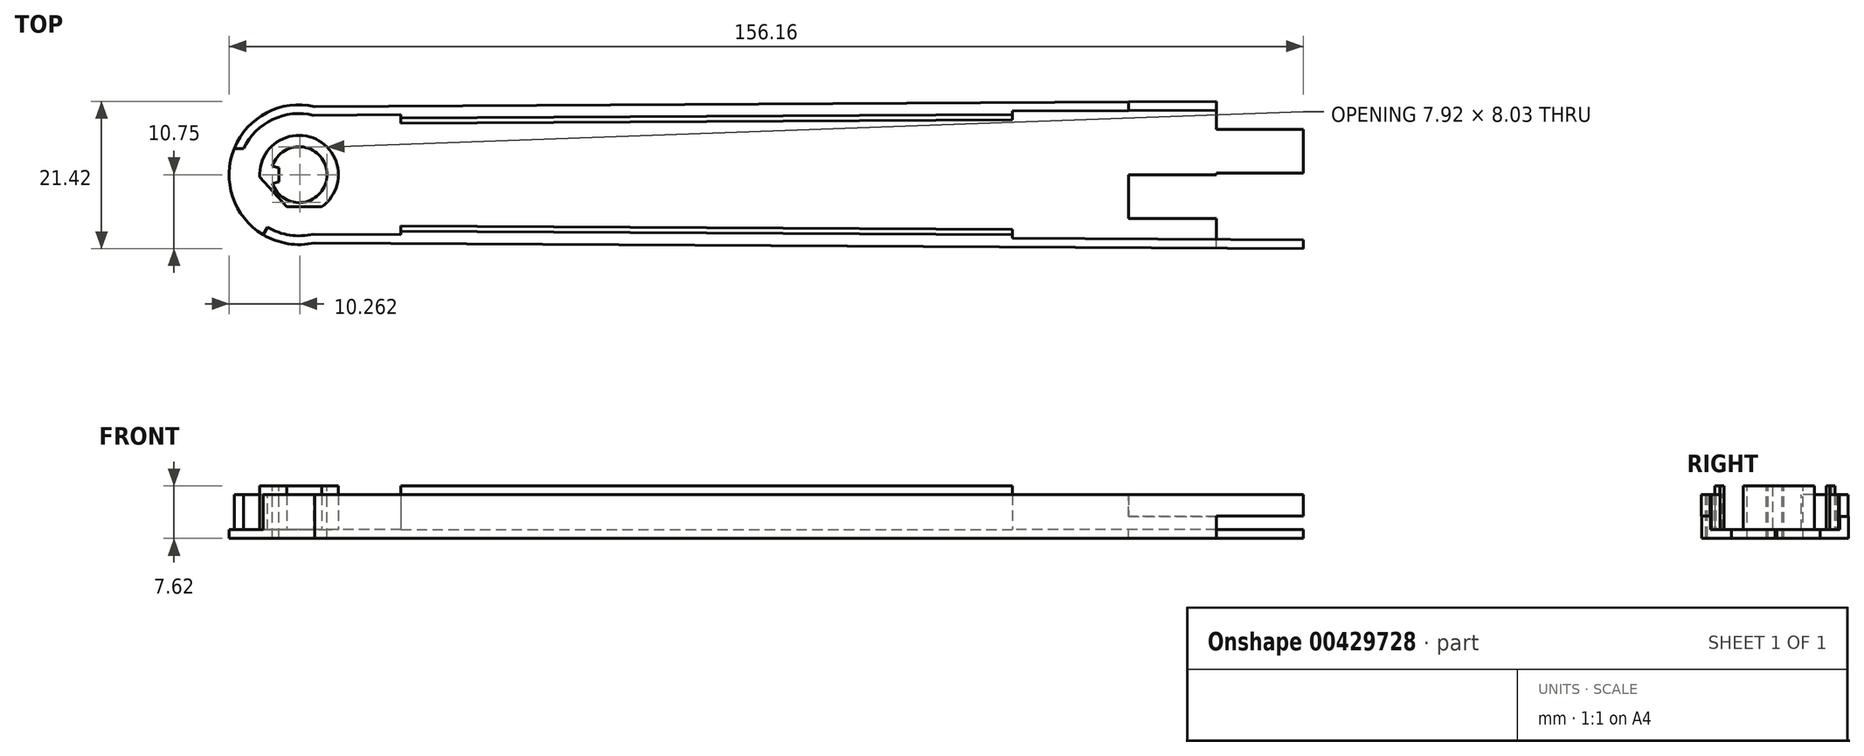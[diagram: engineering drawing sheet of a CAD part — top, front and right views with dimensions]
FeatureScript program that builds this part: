
annotation { "Feature Type Name" : "Feature", "Feature Type Description" : "" }
export const myFeature = defineFeature(function(context is Context, id is Id, definition is map)
    precondition{}
    {
        {
            var Q0;
            Q0=qCreatedBy(makeId("Top.planeOp"),FACE);
            var sketch = newSketch(context, id + "F0", { "sketchPlane" : qUnion([Q0])});
            skPoint(sketch, "E0", {"position": v(-133.35, 0) * mm});
            skPoint(sketch, "E1", {"position": v(133.35, 0) * mm});
            skCircle(sketch, "E2", {"center": v(-133.35, 0) * mm, "radius": 10.16 * mm});
            skCircle(sketch, "E3", {"center": v(133.35, 0) * mm, "radius": 12.07 * mm});
            skPoint(sketch, "E4", {"position": v(-131.1, 9.9) * mm});
            skPoint(sketch, "E5", {"position": v(-131.1, -9.9) * mm});
            skPoint(sketch, "E6", {"position": v(129.49, 11.43) * mm});
            skPoint(sketch, "E7", {"position": v(129.49, -11.43) * mm});
            skLineSegment(sketch, "E8", {"start": v(129.49, 11.43) * mm, "end": v(-131.1, 9.9) * mm});
            skLineSegment(sketch, "E9", {"start": v(129.49, -11.43) * mm, "end": v(-131.1, -9.9) * mm});
            skPoint(sketch, "E10", {"position": v(0, 21.22) * mm});
            skPoint(sketch, "E11", {"position": v(0, -23.02) * mm});
            skLineSegment(sketch, "E12", {"start": v(0, 21.22) * mm, "end": v(0, -23.02) * mm});
            skSolve(sketch);
        }
        {
            var Q0;
            {var subQ0=sQuery(id+"F0.wireOp",EDGE,"E2");var subQ1=makeQuery(id+"F0.imprint","INTERSECT",VERTEX,{"derivedFrom":[subQ0,sQuery(id+"F0.wireOp",EDGE,"E8")]});Q0=makeQuery(id+"F0.imprint","IMPRINT",FACE,{"disambiguationData":[TD([[makeQuery(id+"F0.imprint","IMPRINT",EDGE,{"disambiguationData":[TD([[subQ1,-1.0]])],"derivedFrom":subQ0}),1.0]])]});}
            var Q1;
            {var subQ0=sQuery(id+"F0.wireOp",EDGE,"E8");var subQ1=sQuery(id+"F0.wireOp",EDGE,"E2");var subQ2=makeQuery(id+"F0.imprint","INTERSECT",VERTEX,{"derivedFrom":[subQ1,subQ0]});Q1=makeQuery(id+"F0.imprint","IMPRINT",FACE,{"disambiguationData":[TD([[makeQuery(id+"F0.imprint","IMPRINT",EDGE,{"disambiguationData":[TD([[subQ2,1.0]])],"derivedFrom":subQ1}),-1.0]])]});}
            extrude(context, id + "F1", {"entities" : qUnion([Q0, Q1]), "depth" : 6.35 * mm});
        }
        {
            var Q0;
            Q0=makeQuery(id+"F1.opExtrude","CAP_FACE",FACE,{"disambiguationData":[OSD([sQuery(id+"F0.wireOp",EDGE,"E2"),sQuery(id+"F0.wireOp",EDGE,"E8"),sQuery(id+"F0.wireOp",EDGE,"E9"),sQuery(id+"F0.wireOp",EDGE,"E12")])],"isStart":false});
            var Q1;
            Q1=makeQuery(id+"F1.opExtrude","SWEPT_FACE",FACE,{"disambiguationData":[OSD([sQuery(id+"F0.wireOp",EDGE,"E12")])]});
            shell(context, id + "F2", {"entities" : qUnion([Q0, Q1]), "thickness" : 1.27 * mm});
        }
        {
            var Q0;
            Q0=makeQuery(id+"F2.opShell","OFFSET_FACE",FACE,{"disambiguationData":[OSD([sQuery(id+"F0.wireOp",EDGE,"E2"),sQuery(id+"F0.wireOp",EDGE,"E8"),sQuery(id+"F0.wireOp",EDGE,"E9"),sQuery(id+"F0.wireOp",EDGE,"E12")])]});
            var sketch = newSketch(context, id + "F3", { "sketchPlane" : qUnion([Q0])});
            skLineSegment(sketch, "E13.bottom", {"start": v(0, 0) * mm, "end": v(-12.75, 0) * mm});
            skLineSegment(sketch, "E13.top", {"start": v(0, -6.35) * mm, "end": v(-12.75, -6.35) * mm});
            skLineSegment(sketch, "E13.left", {"start": v(0, 0) * mm, "end": v(0, -6.35) * mm});
            skLineSegment(sketch, "E13.right", {"start": v(-12.75, 0) * mm, "end": v(-12.75, -6.35) * mm});
            skSolve(sketch);
        }
        {
            var Q0;
            Q0=makeQuery(id+"F3.imprint","IMPRINT",FACE,{"disambiguationData":[TD([[makeQuery(id+"F3.imprint","IMPRINT",EDGE,{"derivedFrom":sQuery(id+"F3.wireOp",EDGE,"E13.bottom")}),1.0]])]});
            extrude(context, id + "F4", {"entities" : qUnion([Q0]), "operationType" : NewBodyOperationType.REMOVE, "oppositeDirection" : true, "depth" : 25.4 * mm});
        }
        {
            var Q0;
            Q0=makeQuery(id+"F2.opShell","OFFSET_FACE",FACE,{"disambiguationData":[OSD([sQuery(id+"F0.wireOp",EDGE,"E2"),sQuery(id+"F0.wireOp",EDGE,"E8"),sQuery(id+"F0.wireOp",EDGE,"E9"),sQuery(id+"F0.wireOp",EDGE,"E12")])]});
            var sketch = newSketch(context, id + "F5", { "sketchPlane" : qUnion([Q0])});
            skPoint(sketch, "E14", {"position": v(0, 0.25) * mm});
            skLineSegment(sketch, "E15.bottom", {"start": v(0, 0.25) * mm, "end": v(12.65, 0.25) * mm});
            skLineSegment(sketch, "E15.top", {"start": v(0, 6.58) * mm, "end": v(12.65, 6.58) * mm});
            skLineSegment(sketch, "E15.left", {"start": v(0, 0.25) * mm, "end": v(0, 6.58) * mm});
            skLineSegment(sketch, "E15.right", {"start": v(12.65, 0.25) * mm, "end": v(12.65, 6.58) * mm});
            skSolve(sketch);
        }
        {
            var Q0;
            Q0=makeQuery(id+"F5.imprint","IMPRINT",FACE,{"disambiguationData":[TD([[makeQuery(id+"F5.imprint","IMPRINT",EDGE,{"derivedFrom":sQuery(id+"F5.wireOp",EDGE,"E15.bottom")}),1.0]])]});
            extrude(context, id + "F6", {"entities" : qUnion([Q0]), "operationType" : NewBodyOperationType.ADD, "oppositeDirection" : true, "depth" : 1.27 * mm});
        }
        {
            var Q0;
            Q0=makeQuery(id+"F2.opShell","OFFSET_FACE",FACE,{"disambiguationData":[OSD([sQuery(id+"F0.wireOp",EDGE,"E9")])]});
            var sketch = newSketch(context, id + "F7", { "sketchPlane" : qUnion([Q0])});
            skLineSegment(sketch, "E16.bottom", {"start": v(-0.05, 6.35) * mm, "end": v(-12.7, 6.35) * mm});
            skLineSegment(sketch, "E16.top", {"start": v(-0.05, 3.23) * mm, "end": v(-12.7, 3.23) * mm});
            skLineSegment(sketch, "E16.left", {"start": v(-0.05, 6.35) * mm, "end": v(-0.05, 3.23) * mm});
            skLineSegment(sketch, "E16.right", {"start": v(-12.7, 6.35) * mm, "end": v(-12.7, 3.23) * mm});
            skSolve(sketch);
        }
        {
            var Q0;
            Q0=makeQuery(id+"F7.imprint","IMPRINT",FACE,{"disambiguationData":[TD([[makeQuery(id+"F7.imprint","IMPRINT",EDGE,{"derivedFrom":sQuery(id+"F7.wireOp",EDGE,"E16.bottom")}),1.0]])]});
            extrude(context, id + "F8", {"entities" : qUnion([Q0]), "operationType" : NewBodyOperationType.ADD, "oppositeDirection" : true, "depth" : 1.27 * mm});
        }
        {
            var Q0;
            Q0=makeQuery(id+"F1.opExtrude","SWEPT_FACE",FACE,{"disambiguationData":[OSD([sQuery(id+"F0.wireOp",EDGE,"E8")])]});
            var sketch = newSketch(context, id + "F9", { "sketchPlane" : qUnion([Q0])});
            skLineSegment(sketch, "E17.bottom", {"start": v(-0.06, 6.35) * mm, "end": v(12.69, 6.35) * mm});
            skLineSegment(sketch, "E17.top", {"start": v(-0.06, 3.18) * mm, "end": v(12.69, 3.18) * mm});
            skLineSegment(sketch, "E17.left", {"start": v(-0.06, 6.35) * mm, "end": v(-0.06, 3.18) * mm});
            skLineSegment(sketch, "E17.right", {"start": v(12.69, 6.35) * mm, "end": v(12.69, 3.18) * mm});
            skSolve(sketch);
        }
        {
            var Q0;
            Q0=makeQuery(id+"F9.imprint","IMPRINT",FACE,{"disambiguationData":[TD([[makeQuery(id+"F9.imprint","IMPRINT",EDGE,{"derivedFrom":sQuery(id+"F9.wireOp",EDGE,"E17.bottom")}),-1.0]])]});
            extrude(context, id + "F10", {"entities" : qUnion([Q0]), "operationType" : NewBodyOperationType.REMOVE, "oppositeDirection" : true, "depth" : 2.54 * mm});
        }
        {
            var Q0;
            Q0=makeQuery(id+"F6.boolean.opBoolean","MERGE",FACE,{"derivedFrom":[makeQuery(id+"F2.opShell","OFFSET_FACE",FACE,{"disambiguationData":[OSD([sQuery(id+"F0.wireOp",EDGE,"E2"),sQuery(id+"F0.wireOp",EDGE,"E8"),sQuery(id+"F0.wireOp",EDGE,"E9"),sQuery(id+"F0.wireOp",EDGE,"E12")])]}),makeQuery(id+"F6.opExtrude","CAP_FACE",FACE,{"disambiguationData":[OSD([sQuery(id+"F5.wireOp",EDGE,"E15.bottom"),sQuery(id+"F5.wireOp",EDGE,"E15.top"),sQuery(id+"F5.wireOp",EDGE,"E15.left"),sQuery(id+"F5.wireOp",EDGE,"E15.right")])],"isStart":true})]});
            var sketch = newSketch(context, id + "F11", { "sketchPlane" : qUnion([Q0])});
            skLineSegment(sketch, "E18", {"start": v(-118.54, 8.7) * mm, "end": v(-29.64, 9.23) * mm});
            skLineSegment(sketch, "E19", {"start": v(-118.54, 7.44) * mm, "end": v(-29.64, 7.96) * mm});
            skLineSegment(sketch, "E20", {"start": v(-29.64, 7.96) * mm, "end": v(-29.64, 9.23) * mm});
            skLineSegment(sketch, "E21", {"start": v(-118.54, 7.44) * mm, "end": v(-118.54, 8.7) * mm});
            skLineSegment(sketch, "E22", {"start": v(-118.54, -8.7) * mm, "end": v(-29.64, -9.23) * mm});
            skLineSegment(sketch, "E23", {"start": v(-118.54, -7.44) * mm, "end": v(-29.64, -7.96) * mm});
            skLineSegment(sketch, "E24", {"start": v(-118.54, -7.44) * mm, "end": v(-118.54, -8.7) * mm});
            skLineSegment(sketch, "E25", {"start": v(-29.64, -7.96) * mm, "end": v(-29.64, -9.23) * mm});
            skSolve(sketch);
        }
        {
            var Q0;
            Q0=makeQuery(id+"F11.imprint","IMPRINT",FACE,{"disambiguationData":[TD([[makeQuery(id+"F11.imprint","IMPRINT",EDGE,{"derivedFrom":sQuery(id+"F11.wireOp",EDGE,"E18")}),1.0]])]});
            var Q1;
            Q1=makeQuery(id+"F11.imprint","IMPRINT",FACE,{"disambiguationData":[TD([[makeQuery(id+"F11.imprint","IMPRINT",EDGE,{"derivedFrom":sQuery(id+"F11.wireOp",EDGE,"E22")}),-1.0]])]});
            extrude(context, id + "F12", {"entities" : qUnion([Q0, Q1]), "operationType" : NewBodyOperationType.ADD, "depth" : 5.08 * mm});
        }
        {
            var Q0;
            Q0=makeQuery(id+"F6.boolean.opBoolean","MERGE",FACE,{"derivedFrom":[makeQuery(id+"F2.opShell","OFFSET_FACE",FACE,{"disambiguationData":[OSD([sQuery(id+"F0.wireOp",EDGE,"E2"),sQuery(id+"F0.wireOp",EDGE,"E8"),sQuery(id+"F0.wireOp",EDGE,"E9"),sQuery(id+"F0.wireOp",EDGE,"E12")])]}),makeQuery(id+"F6.opExtrude","CAP_FACE",FACE,{"disambiguationData":[OSD([sQuery(id+"F5.wireOp",EDGE,"E15.bottom"),sQuery(id+"F5.wireOp",EDGE,"E15.top"),sQuery(id+"F5.wireOp",EDGE,"E15.left"),sQuery(id+"F5.wireOp",EDGE,"E15.right")])],"isStart":true})]});
            var sketch = newSketch(context, id + "F13", { "sketchPlane" : qUnion([Q0])});
            skCircle(sketch, "E26", {"center": v(-133.35, 0) * mm, "radius": 5.72 * mm});
            skPoint(sketch, "E27", {"position": v(-139.05, -0.34) * mm});
            skPoint(sketch, "E28", {"position": v(-130.02, -4.65) * mm});
            skPoint(sketch, "E29", {"position": v(-135.1, -4.65) * mm});
            skLineSegment(sketch, "E30", {"start": v(-139.05, -0.34) * mm, "end": v(-135.1, -4.65) * mm});
            skLineSegment(sketch, "E31", {"start": v(-135.1, -4.65) * mm, "end": v(-130.02, -4.65) * mm});
            skCircle(sketch, "E32", {"center": v(-133.35, 0) * mm, "radius": 4.06 * mm});
            skSolve(sketch);
        }
        {
            var Q0;
            {var subQ0=sQuery(id+"F13.wireOp",EDGE,"E30");Q0=makeQuery(id+"F13.imprint","IMPRINT",FACE,{"disambiguationData":[TD([[makeQuery(id+"F13.imprint","IMPRINT",EDGE,{"derivedFrom":subQ0}),1.0]])]});}
            var Q1;
            Q1=makeQuery(id+"F13.imprint","IMPRINT",FACE,{"disambiguationData":[TD([[makeQuery(id+"F13.imprint","IMPRINT",EDGE,{"derivedFrom":sQuery(id+"F13.wireOp",EDGE,"E32")}),1.0]])]});
            extrude(context, id + "F14", {"entities" : qUnion([Q0, Q1]), "operationType" : NewBodyOperationType.ADD, "depth" : 6.35 * mm});
        }
        {
            var Q0;
            Q0=makeQuery(id+"F14.opExtrude","CAP_FACE",FACE,{"disambiguationData":[OSD([sQuery(id+"F13.wireOp",EDGE,"E26"),sQuery(id+"F13.wireOp",EDGE,"KSTsQ0zC-PDxz-6PK0-GiVB-AzygPapndajD"),sQuery(id+"F13.wireOp",EDGE,"wdBHU8a3-bk62-31aO-teXj-baJQRgUME3HU")])],"isStart":false});
            var sketch = newSketch(context, id + "F15", { "sketchPlane" : qUnion([Q0])});
            skCircle(sketch, "E33", {"center": v(-133.35, 0) * mm, "radius": 4.06 * mm});
            skPoint(sketch, "E34", {"position": v(-137.21, 1.27) * mm});
            skPoint(sketch, "E35", {"position": v(-137.21, -1.27) * mm});
            skPoint(sketch, "E36", {"position": v(-136.25, 1.02) * mm});
            skPoint(sketch, "E37", {"position": v(-136.25, -1.02) * mm});
            skLineSegment(sketch, "E38", {"start": v(-137.21, 1.27) * mm, "end": v(-136.25, 1.02) * mm});
            skLineSegment(sketch, "E39", {"start": v(-136.25, 1.02) * mm, "end": v(-136.25, -1.02) * mm});
            skLineSegment(sketch, "E40", {"start": v(-137.21, -1.27) * mm, "end": v(-136.25, -1.02) * mm});
            skSolve(sketch);
        }
        {
            var Q0;
            {var subQ0=sQuery(id+"F15.wireOp",EDGE,"E38");Q0=makeQuery(id+"F15.imprint","IMPRINT",FACE,{"disambiguationData":[TD([[makeQuery(id+"F15.imprint","IMPRINT",EDGE,{"derivedFrom":subQ0}),1.0]])]});}
            extrude(context, id + "F16", {"entities" : qUnion([Q0]), "operationType" : NewBodyOperationType.REMOVE, "oppositeDirection" : true, "depth" : 25.4 * mm});
        }
        {
            var Q0;
            Q0=makeQuery(id+"F8.boolean.opBoolean","MERGE",FACE,{"derivedFrom":[makeQuery(id+"F1.opExtrude","CAP_FACE",FACE,{"disambiguationData":[OSD([sQuery(id+"F0.wireOp",EDGE,"E2"),sQuery(id+"F0.wireOp",EDGE,"E8"),sQuery(id+"F0.wireOp",EDGE,"E9"),sQuery(id+"F0.wireOp",EDGE,"E12")])],"isStart":false}),makeQuery(id+"F8.opExtrude","SWEPT_FACE",FACE,{"disambiguationData":[OSD([sQuery(id+"F7.wireOp",EDGE,"E16.bottom")])]})]});
            var sketch = newSketch(context, id + "F17", { "sketchPlane" : qUnion([Q0])});
            skPoint(sketch, "E41", {"position": v(-141.38, 3.8) * mm});
            skPoint(sketch, "E42", {"position": v(-137.93, -7.62) * mm});
            skPoint(sketch, "E43", {"position": v(-142.77, 3.8) * mm});
            skPoint(sketch, "E44", {"position": v(-138.58, -8.7) * mm});
            skPoint(sketch, "E45", {"position": v(-133.35, 0) * mm});
            skLineSegment(sketch, "E46", {"start": v(-133.35, 0) * mm, "end": v(-138.58, -8.7) * mm});
            skLineSegment(sketch, "E47", {"start": v(-141.38, 3.8) * mm, "end": v(-142.77, 3.8) * mm});
            skArc(sketch, "E48", {"start": v(-141.38, 3.8) * mm, "mid": v(-141.86, -2.57) * mm, "end": v(-137.93, -7.62) * mm});
            skArc(sketch, "E49", {"start": v(-142.77, 3.8) * mm, "mid": v(-142.99, -3.22) * mm, "end": v(-138.58, -8.7) * mm});
            skSolve(sketch);
        }
        {
            var Q0;
            Q0=makeQuery(id+"F17.imprint","IMPRINT",FACE,{"disambiguationData":[TD([[makeQuery(id+"F17.imprint","IMPRINT",EDGE,{"derivedFrom":sQuery(id+"F17.wireOp",EDGE,"E47")}),1.0]])]});
            var Q1;
            Q1=makeQuery(id+"F6.boolean.opBoolean","MERGE",FACE,{"derivedFrom":[makeQuery(id+"F2.opShell","OFFSET_FACE",FACE,{"disambiguationData":[OSD([sQuery(id+"F0.wireOp",EDGE,"E2"),sQuery(id+"F0.wireOp",EDGE,"E8"),sQuery(id+"F0.wireOp",EDGE,"E9"),sQuery(id+"F0.wireOp",EDGE,"E12")])]}),makeQuery(id+"F6.opExtrude","CAP_FACE",FACE,{"disambiguationData":[OSD([sQuery(id+"F5.wireOp",EDGE,"E15.bottom"),sQuery(id+"F5.wireOp",EDGE,"E15.top"),sQuery(id+"F5.wireOp",EDGE,"E15.left"),sQuery(id+"F5.wireOp",EDGE,"E15.right")])],"isStart":true})]});
            extrude(context, id + "F18", {"entities" : qUnion([Q0]), "operationType" : NewBodyOperationType.REMOVE, "endBound" : BoundingType.UP_TO_SURFACE, "oppositeDirection" : true, "endBoundEntityFace" : qUnion([Q1]), "depth" : 25.4 * mm});
        }
        {
            var Q0;
            {var subQ0=sQuery(id+"F11.wireOp",EDGE,"E25");var subQ1=sQuery(id+"F11.wireOp",EDGE,"E24");var subQ2=sQuery(id+"F11.wireOp",EDGE,"E23");var subQ6=sQuery(id+"F7.wireOp",EDGE,"E16.bottom");var subQ7=sQuery(id+"F0.wireOp",EDGE,"E2");var subQ8=sQuery(id+"F0.wireOp",EDGE,"E9");Q0=makeQuery(id+"F18.boolean.opBoolean","SPLIT",FACE,{"disambiguationData":[TD([makeQuery(id+"F1.opExtrude","SWEPT_FACE",FACE,{"disambiguationData":[OSD([subQ8])]})])],"derivedFrom":makeQuery(id+"F12.boolean.opBoolean","MERGE",FACE,{"derivedFrom":[makeQuery(id+"F8.boolean.opBoolean","MERGE",FACE,{"derivedFrom":[makeQuery(id+"F1.opExtrude","CAP_FACE",FACE,{"disambiguationData":[OSD([subQ7,sQuery(id+"F0.wireOp",EDGE,"E8"),subQ8,sQuery(id+"F0.wireOp",EDGE,"E12")])],"isStart":false}),makeQuery(id+"F8.opExtrude","SWEPT_FACE",FACE,{"disambiguationData":[OSD([subQ6])]})]}),makeQuery(id+"F12.opExtrude","CAP_FACE",FACE,{"disambiguationData":[OSD([sQuery(id+"F11.wireOp",EDGE,"E18"),sQuery(id+"F11.wireOp",EDGE,"E19"),sQuery(id+"F11.wireOp",EDGE,"E20"),sQuery(id+"F11.wireOp",EDGE,"E21")])],"isStart":false}),makeQuery(id+"F12.opExtrude","CAP_FACE",FACE,{"disambiguationData":[OSD([sQuery(id+"F11.wireOp",EDGE,"E22"),subQ2,subQ1,subQ0])],"isStart":false})]})});}
            var sketch = newSketch(context, id + "F19", { "sketchPlane" : qUnion([Q0])});
            skLineSegment(sketch, "E50", {"start": v(-118.54, -7.44) * mm, "end": v(-29.64, -7.96) * mm});
            skLineSegment(sketch, "E51", {"start": v(-29.64, -7.96) * mm, "end": v(-29.64, -8.72) * mm});
            skLineSegment(sketch, "E52", {"start": v(-118.54, -7.44) * mm, "end": v(-118.54, -8.2) * mm});
            skLineSegment(sketch, "E53", {"start": v(-118.54, -8.2) * mm, "end": v(-29.64, -8.72) * mm});
            skLineSegment(sketch, "E54.MirrorCS", {"start": v(-118.54, 7.44) * mm, "end": v(-118.54, 8.2) * mm});
            skLineSegment(sketch, "E55.MirrorCS", {"start": v(-29.64, 7.96) * mm, "end": v(-29.64, 8.72) * mm});
            skLineSegment(sketch, "E56.MirrorCS", {"start": v(-118.54, 7.44) * mm, "end": v(-29.64, 7.96) * mm});
            skLineSegment(sketch, "E57.MirrorCS", {"start": v(-118.54, 8.2) * mm, "end": v(-29.64, 8.72) * mm});
            skSolve(sketch);
        }
        {
            var Q0;
            Q0=makeQuery(id+"F19.imprint","IMPRINT",FACE,{"disambiguationData":[TD([[makeQuery(id+"F19.imprint","IMPRINT",EDGE,{"derivedFrom":sQuery(id+"F19.wireOp",EDGE,"E54.MirrorCS")}),-1.0]])]});
            var Q1;
            Q1=makeQuery(id+"F19.imprint","IMPRINT",FACE,{"disambiguationData":[TD([[makeQuery(id+"F19.imprint","IMPRINT",EDGE,{"derivedFrom":sQuery(id+"F19.wireOp",EDGE,"E50")}),-1.0]])]});
            extrude(context, id + "F20", {"entities" : qUnion([Q0, Q1]), "operationType" : NewBodyOperationType.ADD, "depth" : 1.27 * mm});
        }
    });
